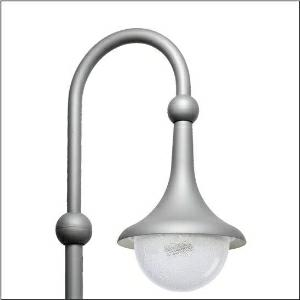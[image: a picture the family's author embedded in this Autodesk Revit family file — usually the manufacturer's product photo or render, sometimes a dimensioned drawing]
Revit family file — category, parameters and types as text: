
# Revit family: grosse_glocke___st1_2a_5xa1563e1b208_1d7c
name_source: partatom
category: Lighting Fixtures
units: mm (PartAtom-declared; Revit-internal decimal feet)

## family parameters
Cut with Voids When Loaded = No
Host = Face
Light Source = No
Part Type = Normal
Room Calculation Point = No
Round Connector Dimension = Use Diameter
Shared = No

## types (1)
- --- (1 x LED, 3210 lm, 23.4 W, 3000K)
    Apparent Load = 23 VA
    CIE Flux Codes = 29 66 94 99 100
    Color Rendering = 70
    Color Temperature = 3000K
    Default Elevation = 1800 mm
    Description = Large Bell, mast luminaire, primary light control with 3 zone facetted reflector, of plastic, silver coated, primary optical cover: enclosure, of PMMA, transparent structured, light distribution: ST1.2a, light emission: direct distribution, primary light characteristic: asymmetric, installation type: suspended mounting, LED, High Power LED, rated luminous flux: 3.210lm, luminous efficacy: 137lm/W, light colour: 730, colour temperature: 3000K, control gear: Plus, control: flexible luminous flux parameterisation, time-dependent luminous flux control, constant luminous flux control, digital communication interface, power reduction, electronic power reduction, mains connection: 230..240V, AC, 50/60Hz, start of lifetime: 23W, end of service life: 24W, reduction: 12W, luminaire housing, bell-shaped, of glass-fibre reinforced polyester, coated, Siteco® metallic grey (DB 702S), please order curved mast extension separately, diameter: 530mm, height: 695mm, mounting height: 4..6m, protection rating (complete): IP54, insulation class (complete): insulation class II (safety insulation), certification: CE, ENEC, VDE, impact resistance: IK08, standard-compliant lighting for roads and squares, packaging unit: 1 piece

Light Distribution: ST1.2a
    Height = 695 mm
    Lamp = 1 x LED
    Lamp Light Flux = 3210 lm
    Lamp Power = 23.4 W
    Lamp count = 1
    Length = 530 mm
    Luminous efficacy = 137 lm/W
    Manufacturer = Siteco
    ModVariant = No
    Model = 5XA1563E1B208
    Number of Poles = 1
    OnlyDefault = Yes
    Power Factor = 1
    Product Name = Große Glocke | ST1.2a
    Product group = mast luminaire | pylon annexe
    ProductGroupID = 6200
    Protection Class = Protection class II
    Protection Degree = IP 54
    RLX_Detail_Level = 1
    RLX_Emergency_Light_Flux = 0 lm
    RLX_Emergency_Type = 0
    RLX_Emergency_Type_DB = No
    RlxData = <blob elided: 54797 chars, md5=149e7dda>
    Socket = socket
    Standby Power = 0 W
    System Light Flux = 3210 lm
    System Power = 23 W
    Type Comments = factory setting: luminous flux: 100 % | dim-lin: 254 | 460 mA
    Type Image = l_1347684.jpg
    URL = http://relux.com
    VarID = @adj_180391
    Voltage = 0 V
    Weight = 0.00 kg
    Width = 0 mm  [stored 0 ft]

note: [stored X ft] marks values corroborated as IEEE doubles in the binary element streams (Revit-internal decimal feet)

## geometry (parser evidence)
native form markers: Blend x4, Sweep x11
no freeform markers — native parametric forms only
